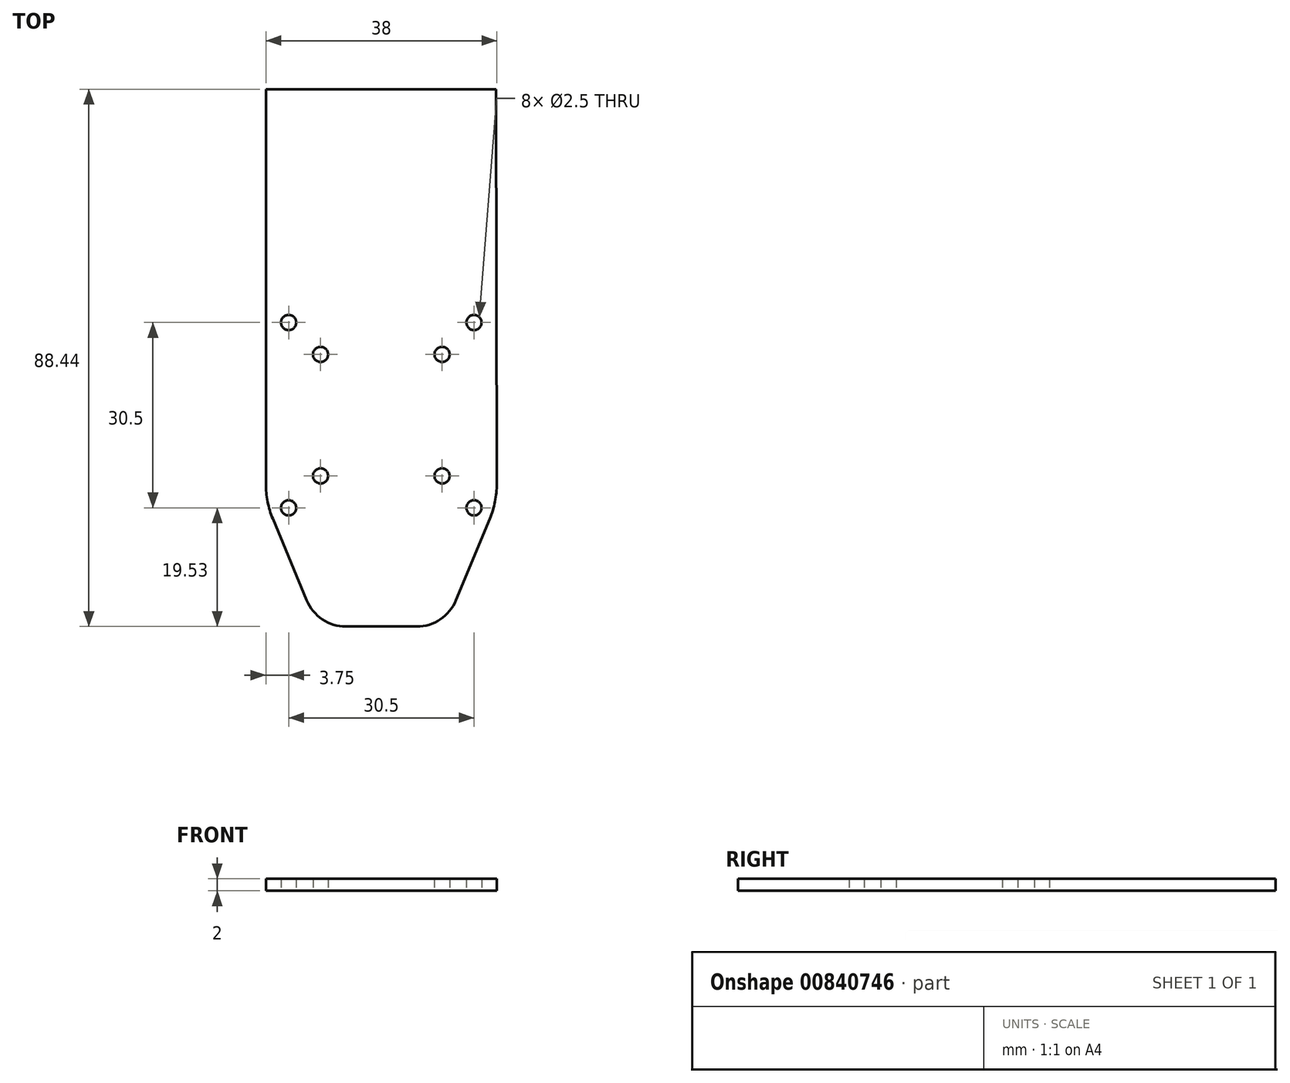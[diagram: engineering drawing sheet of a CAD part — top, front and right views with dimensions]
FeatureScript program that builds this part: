
annotation { "Feature Type Name" : "Feature", "Feature Type Description" : "" }
export const myFeature = defineFeature(function(context is Context, id is Id, definition is map)
    precondition{}
    {
        {
            var Q0;
            Q0=qCreatedBy(makeId("Top.planeOp"),FACE);
            var sketch = newSketch(context, id + "F0", { "sketchPlane" : qUnion([Q0])});
            skLineSegment(sketch, "E0.bottom", {"start": v(10, -10) * mm, "end": v(-10, -10) * mm, "construction": true});
            skLineSegment(sketch, "E0.top", {"start": v(10, 10) * mm, "end": v(-10, 10) * mm, "construction": true});
            skLineSegment(sketch, "E0.left", {"start": v(10, -10) * mm, "end": v(10, 10) * mm, "construction": true});
            skLineSegment(sketch, "E0.right", {"start": v(-10, -10) * mm, "end": v(-10, 10) * mm, "construction": true});
            skPoint(sketch, "E0.middle", {"position": v(0, 0) * mm});
            skCircle(sketch, "E1", {"center": v(-10, 10) * mm, "radius": 1.25 * mm});
            skCircle(sketch, "E2.MirrorC", {"center": v(10, 10) * mm, "radius": 1.25 * mm});
            skCircle(sketch, "E3.MirrorC", {"center": v(10, -10) * mm, "radius": 1.25 * mm});
            skCircle(sketch, "E4.MirrorC", {"center": v(-10, -10) * mm, "radius": 1.25 * mm});
            skPoint(sketch, "E5.right.end.orphan", {"position": v(-13.5, 13.5) * mm});
            skPoint(sketch, "E5.bottom.end.orphan", {"position": v(-13.5, -13.5) * mm});
            skPoint(sketch, "E5.left.end.orphan", {"position": v(13.5, 13.5) * mm});
            skPoint(sketch, "E5.left.start.orphan", {"position": v(13.5, -13.5) * mm});
            skLineSegment(sketch, "E6.bottom", {"start": v(15.25, -15.25) * mm, "end": v(-15.25, -15.25) * mm, "construction": true});
            skLineSegment(sketch, "E6.top", {"start": v(15.25, 15.25) * mm, "end": v(-15.25, 15.25) * mm, "construction": true});
            skLineSegment(sketch, "E6.left", {"start": v(15.25, -15.25) * mm, "end": v(15.25, 15.25) * mm, "construction": true});
            skLineSegment(sketch, "E6.right", {"start": v(-15.25, -15.25) * mm, "end": v(-15.25, 15.25) * mm, "construction": true});
            skCircle(sketch, "E7", {"center": v(-15.25, 15.25) * mm, "radius": 1.25 * mm});
            skCircle(sketch, "E8.MirrorC", {"center": v(15.25, 15.25) * mm, "radius": 1.25 * mm});
            skCircle(sketch, "E9.MirrorC", {"center": v(15.25, -15.25) * mm, "radius": 1.25 * mm});
            skCircle(sketch, "E10.MirrorC", {"center": v(-15.25, -15.25) * mm, "radius": 1.25 * mm});
            skLineSegment(sketch, "E11.top", {"start": v(-19, 53.66) * mm, "end": v(18.87, 53.66) * mm});
            skLineSegment(sketch, "E12", {"start": v(-17.85, -17.05) * mm, "end": v(-14.07, -26.15) * mm});
            skLineSegment(sketch, "E13.MirrorCS", {"start": v(17.85, -17.05) * mm, "end": v(14.07, -26.15) * mm});
            skPoint(sketch, "E14.visualSharp", {"position": v(-19, -14.28) * mm});
            skArc(sketch, "E14.filletArc", {"start": v(-19, -11.3) * mm, "mid": v(-18.71, -14.23) * mm, "end": v(-17.85, -17.05) * mm});
            skLineSegment(sketch, "E15", {"start": v(-5.81, -34.78) * mm, "end": v(5.81, -34.78) * mm});
            skPoint(sketch, "E16.visualSharp", {"position": v(10.49, -34.78) * mm});
            skArc(sketch, "E17.MirrorCS", {"start": v(19, -11.3) * mm, "mid": v(18.71, -14.23) * mm, "end": v(17.85, -17.05) * mm});
            skLineSegment(sketch, "E18", {"start": v(-19, 53.66) * mm, "end": v(-19, -11.3) * mm});
            skLineSegment(sketch, "E19", {"start": v(18.87, 53.66) * mm, "end": v(19, -11.3) * mm});
            skPoint(sketch, "E20.end.orphan", {"position": v(8.94, -30.47) * mm});
            skPoint(sketch, "E21.orphan", {"position": v(-17.85, -17.05) * mm});
            skPoint(sketch, "E22.visualSharp", {"position": v(12.28, -30.47) * mm});
            skArc(sketch, "E23.MirrorCS", {"start": v(5.81, -34.78) * mm, "mid": v(9.7, -33.6) * mm, "end": v(12.28, -30.47) * mm});
            skArc(sketch, "E24.MirrorCS", {"start": v(-5.81, -34.78) * mm, "mid": v(-9.7, -33.6) * mm, "end": v(-12.28, -30.47) * mm});
            skLineSegment(sketch, "E25", {"start": v(-12.28, -30.47) * mm, "end": v(-14.07, -26.15) * mm});
            skLineSegment(sketch, "E26", {"start": v(12.28, -30.47) * mm, "end": v(14.07, -26.15) * mm});
            skSolve(sketch);
        }
        {
            var Q0;
            Q0 = qSketchRegion(id + "F0", true);
            extrude(context, id + "F1", {"entities" : qUnion([Q0]), "depth" : 2 * mm, "offsetDistance" : 25 * mm});
        }
    });
